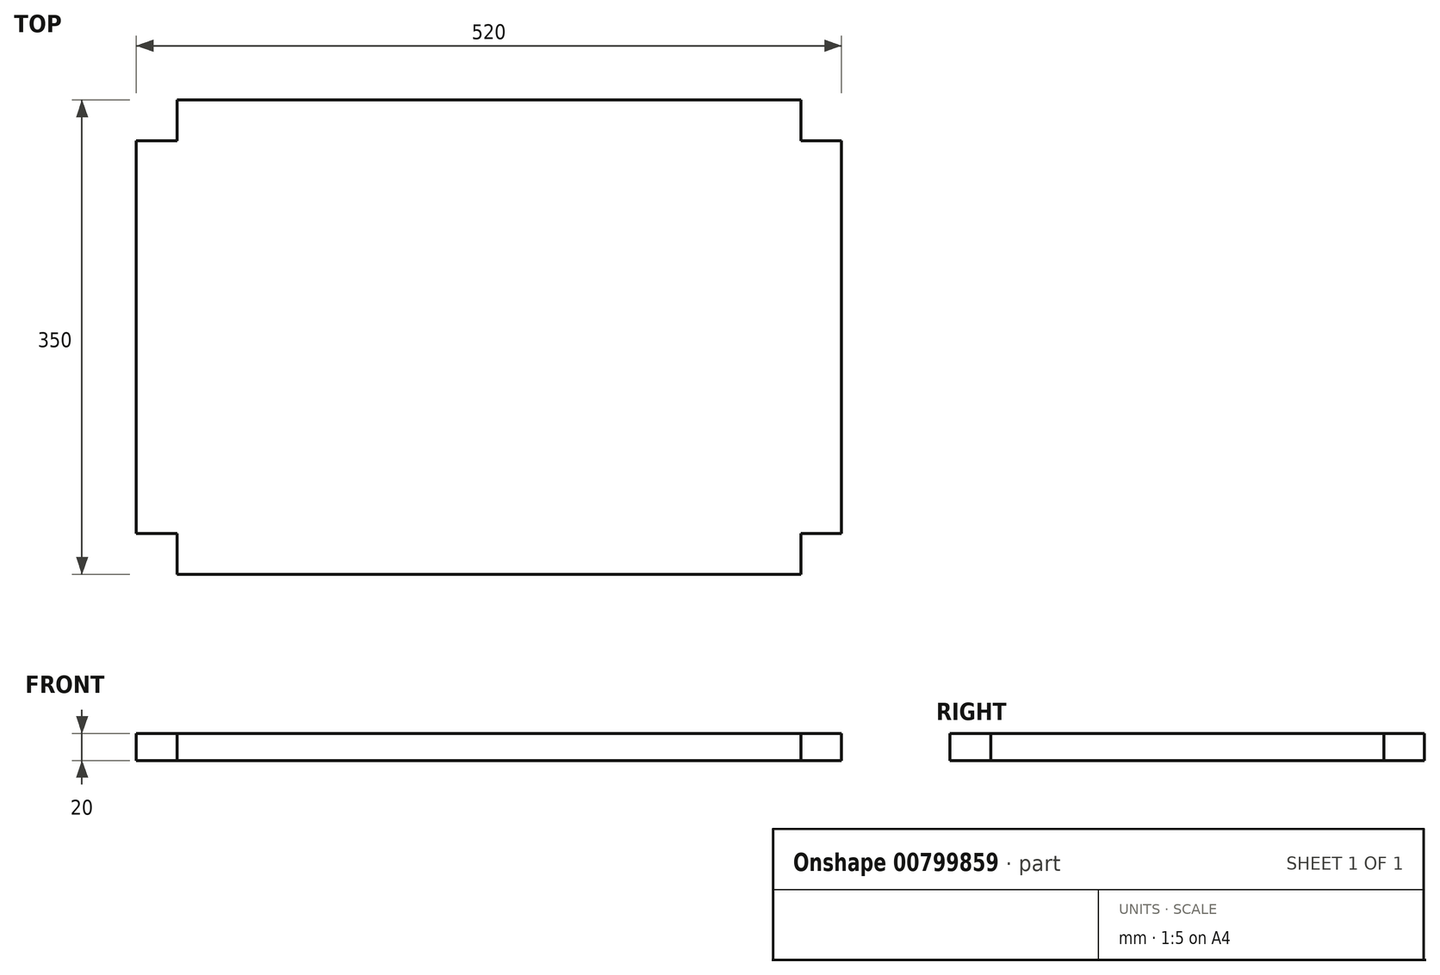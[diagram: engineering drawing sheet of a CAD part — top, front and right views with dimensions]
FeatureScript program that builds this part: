
annotation { "Feature Type Name" : "Feature", "Feature Type Description" : "" }
export const myFeature = defineFeature(function(context is Context, id is Id, definition is map)
    precondition{}
    {
        {
            var Q0;
            Q0=qCreatedBy(makeId("Top.planeOp"),FACE);
            var sketch = newSketch(context, id + "F0", { "sketchPlane" : qUnion([Q0])});
            skLineSegment(sketch, "E0", {"start": v(0, 175) * mm, "end": v(-230, 175) * mm});
            skLineSegment(sketch, "E1", {"start": v(-230, 175) * mm, "end": v(-230, 145) * mm});
            skLineSegment(sketch, "E2", {"start": v(-230, 145) * mm, "end": v(-260, 145) * mm});
            skLineSegment(sketch, "E3", {"start": v(-260, 145) * mm, "end": v(-260, 0) * mm});
            skLineSegment(sketch, "E4.MirrorCS", {"start": v(-260, -145) * mm, "end": v(-260, 0) * mm});
            skLineSegment(sketch, "E5.MirrorCS", {"start": v(0, -175) * mm, "end": v(-230, -175) * mm});
            skLineSegment(sketch, "E6.MirrorCS", {"start": v(-230, -175) * mm, "end": v(-230, -145) * mm});
            skLineSegment(sketch, "E7.MirrorCS", {"start": v(-230, -145) * mm, "end": v(-260, -145) * mm});
            skLineSegment(sketch, "E8.MirrorCS", {"start": v(230, -145) * mm, "end": v(260, -145) * mm});
            skLineSegment(sketch, "E9.MirrorCS", {"start": v(230, -175) * mm, "end": v(230, -145) * mm});
            skLineSegment(sketch, "E10.MirrorCS", {"start": v(260, 145) * mm, "end": v(260, 0) * mm});
            skLineSegment(sketch, "E11.MirrorCS", {"start": v(230, 145) * mm, "end": v(260, 145) * mm});
            skLineSegment(sketch, "E12.MirrorCS", {"start": v(0, -175) * mm, "end": v(230, -175) * mm});
            skLineSegment(sketch, "E13.MirrorCS", {"start": v(0, 175) * mm, "end": v(230, 175) * mm});
            skLineSegment(sketch, "E14.MirrorCS", {"start": v(260, -145) * mm, "end": v(260, 0) * mm});
            skLineSegment(sketch, "E15.MirrorCS", {"start": v(230, 175) * mm, "end": v(230, 145) * mm});
            skSolve(sketch);
        }
        {
            var Q0;
            Q0=makeQuery(id+"F0.imprint","IMPRINT",FACE,{"disambiguationData":[TD([[makeQuery(id+"F0.imprint","IMPRINT",EDGE,{"derivedFrom":sQuery(id+"F0.wireOp",EDGE,"E0")}),1.0]])]});
            extrude(context, id + "F1", {"entities" : qUnion([Q0]), "depth" : 20 * mm, "offsetDistance" : 25 * mm});
        }
    });
